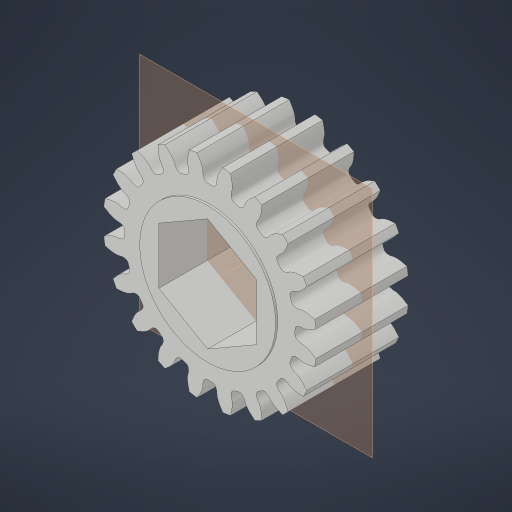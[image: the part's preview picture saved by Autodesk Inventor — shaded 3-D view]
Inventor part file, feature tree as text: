
AUTODESK INVENTOR PART (.ipt)
format: ipt  version: 2023.4 (Build 274418000, 418)  size: 551,936 bytes
history: native  units: in
note: dims shown in document units (in); Inventor stores cm internally (conversion verified against a paired STEP export)
features: plane x1, other x1
ambient origin geometry x8: Origin, YZ Plane, XZ Plane, XY Plane, X Axis, Y Axis, Z Axis, Center Point
bodies: Solid1 (feature_tree)
feature tree (2):
  plane  "Work Plane1"
  other  "Boss-Extrude1"
